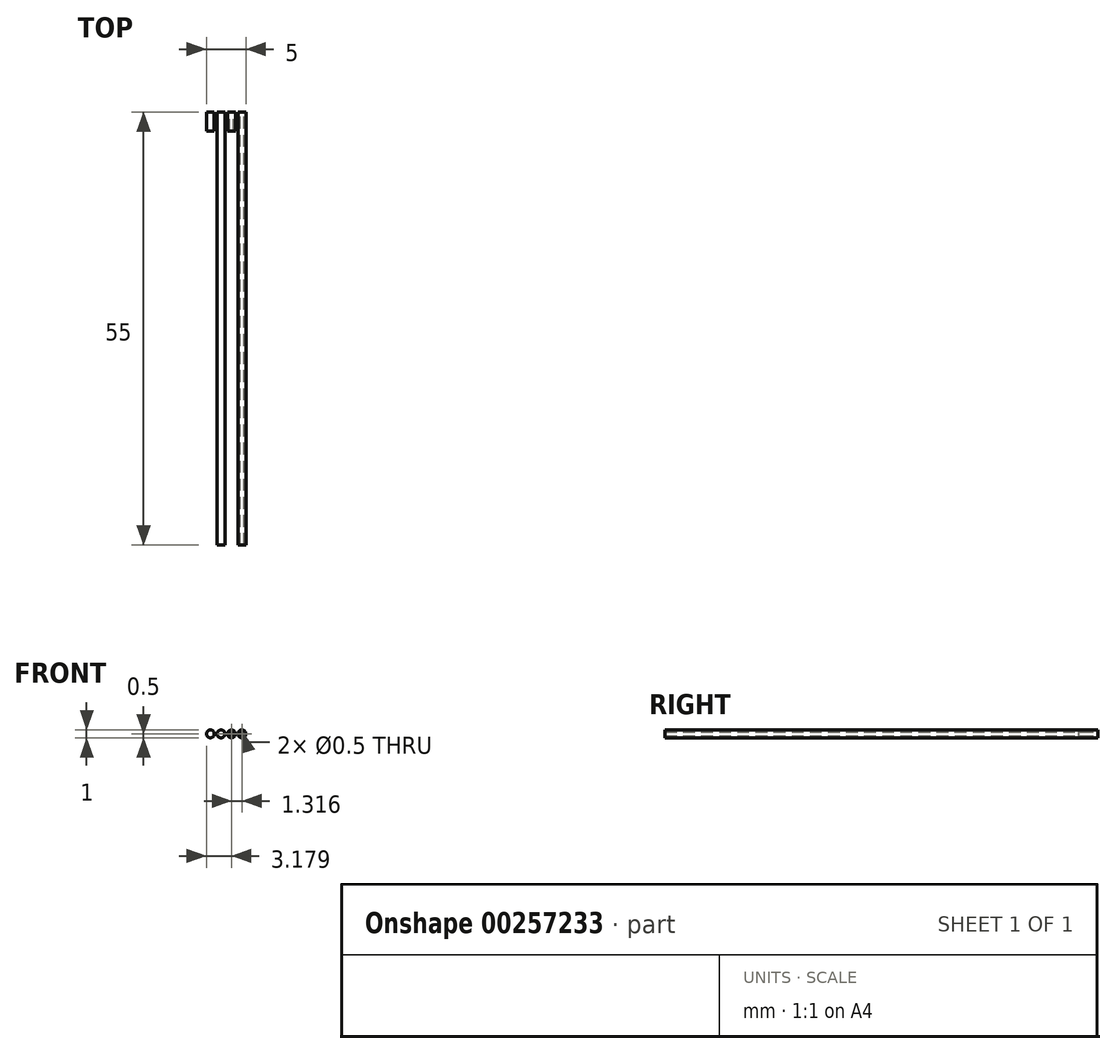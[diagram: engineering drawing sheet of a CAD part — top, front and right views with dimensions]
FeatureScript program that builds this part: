
annotation { "Feature Type Name" : "Feature", "Feature Type Description" : "" }
export const myFeature = defineFeature(function(context is Context, id is Id, definition is map)
    precondition{}
    {
        {
            var Q0;
            Q0=qCreatedBy(makeId("Front.planeOp"),FACE);
            var sketch = newSketch(context, id + "F0", { "sketchPlane" : qUnion([Q0])});
            skCircle(sketch, "E0", {"center": v(0, 0) * mm, "radius": 0.5 * mm});
            skCircle(sketch, "E1", {"center": v(1.33, 0) * mm, "radius": 0.5 * mm});
            skCircle(sketch, "E2", {"center": v(2.65, 0) * mm, "radius": 0.5 * mm});
            skCircle(sketch, "E3", {"center": v(-1.35, 0) * mm, "radius": 0.5 * mm});
            skCircle(sketch, "E4", {"center": v(1.33, 0) * mm, "radius": 0.25 * mm});
            skCircle(sketch, "E5", {"center": v(2.65, 0) * mm, "radius": 0.25 * mm});
            skSolve(sketch);
        }
        {
            var Q0;
            Q0=makeQuery(id+"F0.imprint","IMPRINT",FACE,{"disambiguationData":[TD([[makeQuery(id+"F0.imprint","IMPRINT",EDGE,{"derivedFrom":sQuery(id+"F0.wireOp",EDGE,"E3")}),1.0]])]});
            extrude(context, id + "F1", {"entities" : qUnion([Q0]), "depth" : 2.4 * mm});
        }
        {
            var Q0;
            Q0=makeQuery(id+"F0.imprint","IMPRINT",FACE,{"disambiguationData":[TD([[makeQuery(id+"F0.imprint","IMPRINT",EDGE,{"derivedFrom":sQuery(id+"F0.wireOp",EDGE,"E0")}),1.0]])]});
            extrude(context, id + "F2", {"entities" : qUnion([Q0]), "depth" : 55 * mm});
        }
        {
            var Q0;
            Q0=makeQuery(id+"F0.imprint","IMPRINT",FACE,{"disambiguationData":[TD([[makeQuery(id+"F0.imprint","IMPRINT",EDGE,{"derivedFrom":sQuery(id+"F0.wireOp",EDGE,"E1")}),1.0]])]});
            extrude(context, id + "F3", {"entities" : qUnion([Q0]), "depth" : 2.4 * mm});
        }
        {
            var Q0;
            Q0=makeQuery(id+"F0.imprint","IMPRINT",FACE,{"disambiguationData":[TD([[makeQuery(id+"F0.imprint","IMPRINT",EDGE,{"derivedFrom":sQuery(id+"F0.wireOp",EDGE,"E2")}),1.0]])]});
            extrude(context, id + "F4", {"entities" : qUnion([Q0]), "depth" : 55 * mm});
        }
    });
